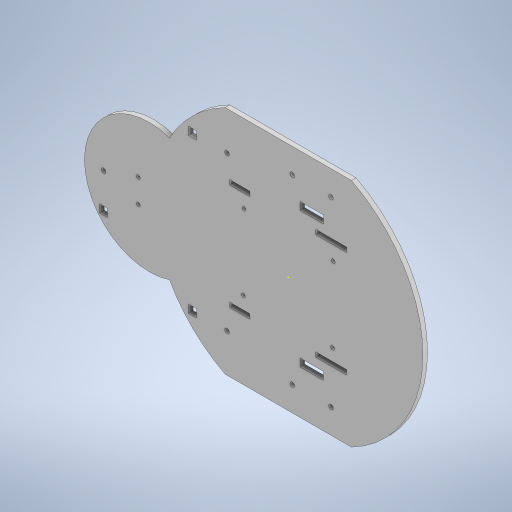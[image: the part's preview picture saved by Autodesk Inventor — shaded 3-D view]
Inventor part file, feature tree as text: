
AUTODESK INVENTOR PART (.ipt)
format: ipt  version: 2023 (Build 270158000, 158)  size: 363,520 bytes
history: native  units: in
note: dims shown in document units (in); Inventor stores cm internally (conversion verified against a paired STEP export)
features: extrude x8, other x8, sketch x5, reference x4, hole x2, mirror x2, imported_body x1
ambient origin geometry x8: Origin, YZ Plane, XZ Plane, XY Plane, X Axis, Y Axis, Z Axis, Center Point
bodies: Body1 (feature_tree)
feature tree (30):
  imported_body  "Base"
  hole  "Holes and Mounts"  [1 undecoded]
  extrude  "ComponentARBHoles"  Depth=0.3937in TaperAngle=0.0deg
  extrude  "WheelFrontSensorHoles"  Depth=3.4449in
  other  "SensorHolesSidesSketch"
  sketch  "Sketch9"  dims[d53=0.1181in d54=0.2047in d55=0.2047in d62=1.1811in]
  extrude  "HolderSlots"  Depth=0.3937in TaperAngle=0.0deg
  extrude  "MagnetHoleBottom"  Depth=0.1969in
  extrude  "MagnetHoleSides"  Depth=0.0591in TaperAngle=0.0deg
  extrude  "Extrusion10"  Depth=0.0591in TaperAngle=0.0deg
  mirror  "Mirror2"
  extrude  "Ball Caster Holes"  Depth=0.3937in TaperAngle=0.0deg
  extrude  "Extrusion12"  Depth=0.1969in
  mirror  "Mirror3"
  reference  "Reference1"
  reference  "Reference2"
  reference  "Reference3"
  reference  "Reference4"
  hole  "Holes Only"  [1 undecoded]
  other  "HolderSlotsSketch"
  sketch  "Sketch11"  dims[d67=0.1181in d68=0.0in d80=0.3937in d81=0.0in]
  sketch  "Sketch13"  dims[d84=3.4449in d85=2.9551in]
  sketch  "Sketch14"  dims[d88=1.6581in d98=0.3937in d99=0.0in]
  sketch  "Sketch15"  dims[d100=6.4173in d101=0.1575in d102=0.0591in d103=0.0in d110=0.0591in d111=0.0in d117=0.3937in d118=0.0in d120=0.0984in d121=0.0984in d122=0.1in d123=0.1in d126=0.3937in d127=0.0in d131=0.3937in d132=0.0in d44=0.1969in d45=0.0344in d46=0.1969in d47=0.0344in d48=0.1969in d49=0.0344in]
  parser-record x1  (decoder bookkeeping rows leaked as tree rows — omitted from the tree; the rows remain in map.json)
  other  "Ladybirdbot.iam"
  other  "M2.5 Hex Spacer 5mm:1"
  other  "M2.5 Hex Spacer 5mm:2"
  other  "M2.5 Hex Spacer 5mm:4"
  other  "M2.5 Hex Spacer 5mm:3"
note: 2 required parameter values undecoded (feature->parameter linkage not recoverable at this tier; creation-order binding heuristic only, values carry confidence <= 0.55)
note: 1 file-system path scrubbed to <path> (originals preserved in map.json)
